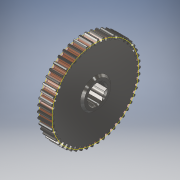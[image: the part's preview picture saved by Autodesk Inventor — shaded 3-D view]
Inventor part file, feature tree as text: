
AUTODESK INVENTOR PART (.ipt)
format: ipt  version: 2018 (Build 220112000, 112)  size: 359,936 bytes
history: native  units: in
note: dims shown in document units (in); Inventor stores cm internally (conversion verified against a paired STEP export)
features: other x4, sketch x1
ambient origin geometry x8: Origin, YZ Plane, XZ Plane, XY Plane, X Axis, Y Axis, Z Axis, Center Point
bodies: Solid1 (feature_tree)
feature tree (5):
  other  "Repaired Geometry1"
  sketch  "Sketch1"  dims[d0=2.5in d1=1.0in d2=0.0in]
  other  "Srf1"
  other  "Cut-Extrude3"
  other  "pitch circle"
